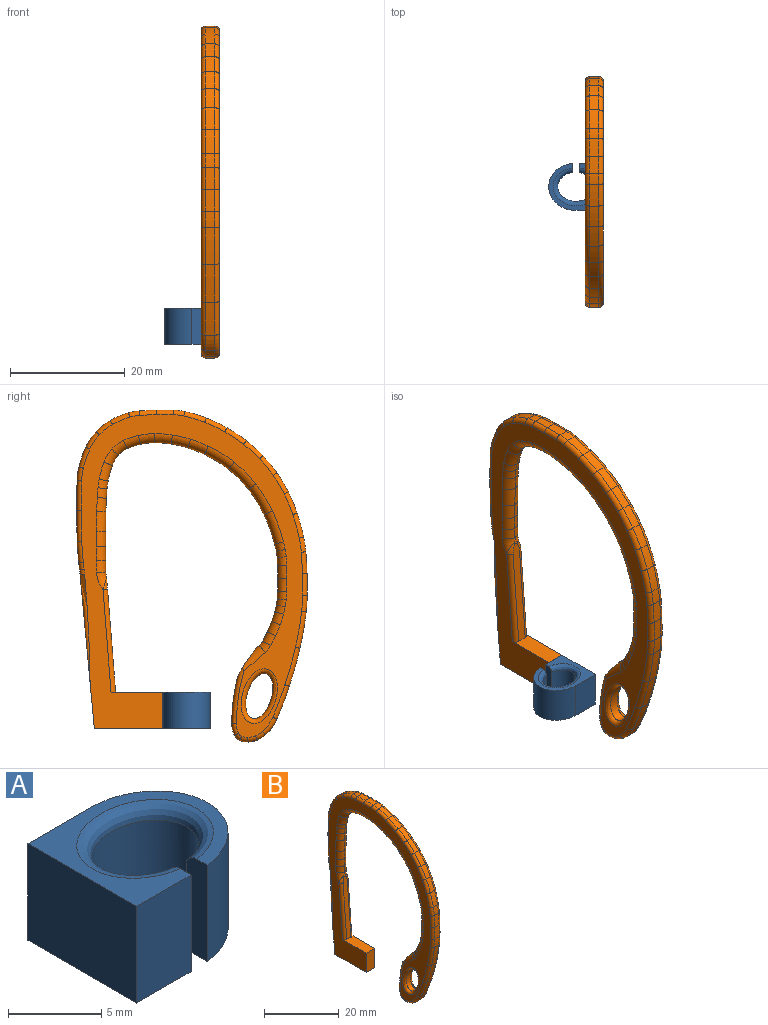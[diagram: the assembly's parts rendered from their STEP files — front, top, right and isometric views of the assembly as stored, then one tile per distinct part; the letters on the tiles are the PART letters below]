
ASSEMBLY  parts=2 mates=1
PART A: 10 faces, bbox 9.6x8.3x6.4 mm
  f0: plane 6.4x1.68mm, normal (1,0,0), area 10.3mm2, adj f1,f6,f7,f8,f9
  f1: extruded ~6.33x5.56mm, area 93mm2, adj f0,f2,f8,f9
  f2: plane 6.4x1.65mm, normal (-1,0,0), area 10mm2, adj f1,f3,f7,f8,f9
  f3: extruded ~8.22x6.35mm, area 84.7mm2, adj f2,f4,f7,f8
  f4: plane 6.35x4.76mm, normal (0,1,0), area 30.2mm2, adj f3,f5,f7,f8
  f5: plane 8.26x6.35mm, normal (-1,0,0), area 52.4mm2, adj f4,f6,f7,f8
  f6: plane 6.35x4.13mm, normal (0,-1,0), area 26.2mm2, adj f0,f5,f7,f8
  f7: plane 9.53x8.26mm, normal (0,0,1), area 27.6mm2, adj f0,f2,f3,f4,f5,f6,f9
  f8: plane 9.53x8.26mm, normal (0,0,-1), area 42.8mm2, adj f0,f1,f2,f3,f4,f5,f6
  f9: bspline ~7.95x6.67mm, area 23.2mm2, adj f0,f1,f2,f7
PART B: 200 faces, bbox 3.8x40.5x58.5 mm
  f0: plane 26.17x3.41mm, normal (0,1,-0.09), area 72.5mm2, adj f1,f47,f48,f49,f124,f157
  f1: cylinder r=232.47mm len=1.59mm, axis (-1,0,0), area 1.3mm2, adj f0,f2,f124,f157
  f2: cylinder r=58.84mm len=1.59mm, axis (-1,0,0), area 1.5mm2, adj f1,f3,f126,f158
  f3: cylinder r=110.76mm len=1.59mm, axis (-1,0,0), area 1.8mm2, adj f2,f4,f128,f159
  f4: cylinder r=45.01mm len=3.81mm, axis (-1,0,0), area 6.1mm2, adj f3,f5,f130,f160
  f5: cylinder r=168.97mm len=5.36mm, axis (-1,0,0), area 8.5mm2, adj f4,f6,f132,f161
  f6: cylinder r=210.56mm len=5.24mm, axis (-1,0,0), area 8.3mm2, adj f5,f7,f134,f162
  f7: cylinder r=11.54mm len=2.35mm, axis (-1,0,0), area 3.8mm2, adj f6,f8,f136,f163
  f8: cylinder r=18.11mm len=3.5mm, axis (-1,0,0), area 5.9mm2, adj f7,f9,f138,f164
  f9: cylinder r=10.63mm len=2.69mm, axis (-1,0,0), area 5.2mm2, adj f8,f10,f140,f165
  f10: cylinder r=9.99mm len=2.47mm, axis (-1,0,0), area 5mm2, adj f9,f11,f142,f166
  f11: cylinder r=14.59mm len=3.2mm, axis (-1,0,0), area 5.5mm2, adj f10,f12,f144,f167
  f12: cylinder r=9.3mm len=1.84mm, axis (-1,0,0), area 3mm2, adj f11,f13,f146,f168
  f13: cylinder r=58.67mm len=3.02mm, axis (-1,0,0), area 4.8mm2, adj f12,f14,f148,f169
  f14: cylinder r=58.13mm len=3.04mm, axis (-1,0,0), area 4.8mm2, adj f13,f15,f150,f170
  f15: cylinder r=10.16mm len=1.91mm, axis (-1,0,0), area 3.1mm2, adj f14,f16,f152,f171
  f16: cylinder r=25.74mm len=3.75mm, axis (-1,0,0), area 6.2mm2, adj f15,f17,f154,f172
  f17: cylinder r=28.28mm len=3.63mm, axis (-1,0,0), area 6.4mm2, adj f16,f18,f156,f173
  f18: cylinder r=28.2mm len=3.34mm, axis (-1,0,0), area 6.4mm2, adj f17,f19,f155,f174
  f19: cylinder r=25.35mm len=2.9mm, axis (-1,0,0), area 6.2mm2, adj f18,f20,f153,f175
  f20: cylinder r=26.11mm len=2.99mm, axis (-1,0,0), area 6.1mm2, adj f19,f21,f151,f176
  f21: cylinder r=26.17mm len=3.32mm, axis (-1,0,0), area 6.1mm2, adj f20,f22,f149,f177
  f22: cylinder r=28.64mm len=3.72mm, axis (-1,0,0), area 6.4mm2, adj f21,f23,f147,f178
  f23: cylinder r=38.83mm len=4.19mm, axis (-1,0,0), area 6.9mm2, adj f22,f24,f145,f179
  f24: cylinder r=19.44mm len=2.55mm, axis (-1,0,0), area 4.1mm2, adj f23,f25,f143,f180
  f25: cylinder r=82.96mm len=3.74mm, axis (-1,0,0), area 5.9mm2, adj f24,f26,f141,f181
  f26: cylinder r=82.89mm len=3.83mm, axis (-1,0,0), area 6.1mm2, adj f25,f27,f139,f182
  f27: cylinder r=28.77mm len=2.92mm, axis (-1,0,0), area 4.6mm2, adj f26,f28,f137,f183
  f28: cylinder r=57.68mm len=6.36mm, axis (-1,0,0), area 10.2mm2, adj f27,f29,f135,f184
  f29: cylinder r=74.7mm len=6.63mm, axis (-1,0,0), area 10.9mm2, adj f28,f30,f133,f185
  f30: cylinder r=71.53mm len=5.73mm, axis (-1,0,0), area 9.7mm2, adj f29,f31,f131,f186
  f31: cylinder r=7.91mm len=2.76mm, axis (-1,0,0), area 5.4mm2, adj f30,f32,f129,f187
  f32: cylinder r=4.84mm len=1.59mm, axis (-1,0,0), area 2.7mm2, adj f31,f33,f127,f188
  f33: cylinder r=4.59mm len=1.63mm, axis (-1,0,0), area 2.7mm2, adj f32,f34,f125,f189
  f34: cylinder r=3.45mm len=1.59mm, axis (-1,0,0), area 2.3mm2, adj f33,f35,f123,f190
  f35: cylinder r=1.84mm len=1.59mm, axis (-1,0,0), area 2mm2, adj f34,f36,f122,f191
  f36: cylinder r=4.49mm len=2.09mm, axis (-1,0,0), area 3.4mm2, adj f35,f37,f121,f192
  f37: cylinder r=34.45mm len=3.69mm, axis (-1,0,0), area 5.9mm2, adj f36,f38,f120,f193
  f38: cylinder r=33.33mm len=3.71mm, axis (-1,0,0), area 6.2mm2, adj f37,f39,f119,f193
  f39: cylinder r=7.14mm len=2.32mm, axis (-1,0,0), area 5mm2, adj f38,f40,f83,f118,f193
  f40: cylinder r=15.1mm len=2.25mm, axis (-1,0,0), area 1.3mm2, adj f39,f41,f83,f116,f117
  f41: plane 2.99x2.51mm, normal (0,0.81,0.59), area 6.9mm2, adj f40,f50,f83,f116
  f42: plane 0.84x0.83mm, normal (0,-0.99,0.17), area 0.3mm2, adj f43,f82,f115,f197,f199
  f43: plane 19.7x1.59mm, normal (0,-1,0.08), area 30.8mm2, adj f42,f44,f196,f197,f198,f199
  f44: plane 9.07x3.2mm, normal (0,0,1), area 26.5mm2, adj f43,f45,f48,f49,f196,f198
  f45: plane 6.32x3.18mm, normal (0,-1,0), area 20.1mm2, adj f44,f47,f48,f49
  f46: extruded ~7.93x4.75mm, area 31.9mm2, adj f194,f195
  f47: plane 11.95x3.18mm, normal (0,0,-1), area 37.9mm2, adj f0,f45,f48,f49
  f48: plane 56.33x38.63mm, normal (1,0,0), area 465.9mm2, adj f0,f44,f45,f47,f50,f51,f52,f53
  f49: plane 56.33x38.63mm, normal (-1,0,0), area 466.1mm2, adj f0,f44,f45,f47,f83,f84,f85,f86
  f50: cylinder r=1.59mm len=4.13mm, axis (0,0.75,-0.67), area 5.9mm2, adj f41,f48,f51,f83,f116
  f51: torus R=4.44mm, axis (1,0,0), area 2.9mm2, adj f48,f50,f52,f84
  f52: torus R=29.43mm, axis (1,0,0), area 4.6mm2, adj f48,f51,f53,f85
  f53: torus R=28.92mm, axis (1,0,0), area 5mm2, adj f48,f52,f54,f86
  f54: torus R=18.86mm, axis (1,0,0), area 4.5mm2, adj f48,f53,f55,f87
  f55: torus R=17.58mm, axis (1,0,0), area 3.1mm2, adj f48,f54,f56,f88
  f56: torus R=12.41mm, axis (1,0,0), area 2.9mm2, adj f48,f55,f57,f89
  f57: torus R=21.42mm, axis (1,0,0), area 3.5mm2, adj f48,f56,f58,f90
  f58: torus R=135.56mm, axis (1,0,0), area 5.6mm2, adj f48,f57,f59,f91
  f59: torus R=133.92mm, axis (1,0,0), area 5.6mm2, adj f48,f58,f60,f92
  f60: torus R=21.45mm, axis (1,0,0), area 3.5mm2, adj f48,f59,f61,f93
  f61: torus R=12.86mm, axis (1,0,0), area 2.9mm2, adj f48,f60,f62,f94
  f62: torus R=19.98mm, axis (1,0,0), area 3.2mm2, adj f48,f61,f63,f95
  f63: torus R=31.27mm, axis (1,0,0), area 14mm2, adj f48,f62,f64,f96
  f64: torus R=24.44mm, axis (1,0,0), area 13.2mm2, adj f48,f63,f65,f97
  f65: torus R=22.66mm, axis (1,0,0), area 12.7mm2, adj f48,f64,f66,f98
  f66: torus R=22.82mm, axis (1,0,0), area 12.7mm2, adj f48,f65,f67,f99
  f67: torus R=25.24mm, axis (1,0,0), area 8mm2, adj f48,f66,f68,f100
  f68: torus R=21.78mm, axis (1,0,0), area 7.7mm2, adj f48,f67,f69,f101
  f69: torus R=19.33mm, axis (1,0,0), area 7.2mm2, adj f48,f68,f70,f102
  f70: torus R=14mm, axis (1,0,0), area 6.7mm2, adj f48,f69,f71,f103
  f71: torus R=12.52mm, axis (1,0,0), area 6.3mm2, adj f48,f70,f72,f104
  f72: torus R=6.19mm, axis (1,0,0), area 5.5mm2, adj f48,f71,f73,f105
  f73: torus R=7.08mm, axis (1,0,0), area 5.7mm2, adj f48,f72,f74,f106
  f74: torus R=20.17mm, axis (1,0,0), area 7.3mm2, adj f48,f73,f75,f107
  f75: torus R=16.03mm, axis (1,0,0), area 3.4mm2, adj f48,f74,f76,f108
  f76: torus R=37.03mm, axis (1,0,0), area 4.2mm2, adj f48,f75,f77,f109
  f77: torus R=75.32mm, axis (1,0,0), area 5.8mm2, adj f48,f76,f78,f110
  f78: torus R=374.9mm, axis (1,0,0), area 8.8mm2, adj f48,f77,f79,f111
  f79: torus R=368.87mm, axis (1,0,0), area 6.7mm2, adj f48,f78,f80,f112
  f80: torus R=230.02mm, axis (1,0,0), area 5.9mm2, adj f48,f79,f81,f113
  f81: torus R=353.05mm, axis (1,0,0), area 5mm2, adj f48,f80,f82,f114
  f82: torus R=4.98mm, axis (1,0,0), area 4.5mm2, adj f42,f48,f81,f115,f199
  f83: cylinder r=1.59mm len=4.8mm, axis (0,-0.75,0.67), area 7.2mm2, adj f39,f40,f41,f49,f50,f84,f193
  f84: torus R=4.44mm, axis (1,0,0), area 2.9mm2, adj f49,f51,f83,f85
  f85: torus R=29.43mm, axis (1,0,0), area 4.6mm2, adj f49,f52,f84,f86
  f86: torus R=28.92mm, axis (1,0,0), area 5mm2, adj f49,f53,f85,f87
  f87: torus R=18.86mm, axis (1,0,0), area 4.5mm2, adj f49,f54,f86,f88
  f88: torus R=17.58mm, axis (1,0,0), area 3.1mm2, adj f49,f55,f87,f89
  f89: torus R=12.41mm, axis (1,0,0), area 2.9mm2, adj f49,f56,f88,f90
  f90: torus R=21.42mm, axis (1,0,0), area 3.5mm2, adj f49,f57,f89,f91
  f91: torus R=135.56mm, axis (1,0,0), area 5.6mm2, adj f49,f58,f90,f92
  f92: torus R=133.92mm, axis (1,0,0), area 5.6mm2, adj f49,f59,f91,f93
  f93: torus R=21.45mm, axis (1,0,0), area 3.5mm2, adj f49,f60,f92,f94
  f94: torus R=12.86mm, axis (1,0,0), area 2.9mm2, adj f49,f61,f93,f95
  f95: torus R=19.98mm, axis (1,0,0), area 3.2mm2, adj f49,f62,f94,f96
  f96: torus R=31.27mm, axis (1,0,0), area 14mm2, adj f49,f63,f95,f97
  f97: torus R=24.44mm, axis (1,0,0), area 13.2mm2, adj f49,f64,f96,f98
  f98: torus R=22.66mm, axis (1,0,0), area 12.7mm2, adj f49,f65,f97,f99
  f99: torus R=22.82mm, axis (1,0,0), area 12.7mm2, adj f49,f66,f98,f100
  f100: torus R=25.24mm, axis (1,0,0), area 8mm2, adj f49,f67,f99,f101
  f101: torus R=21.78mm, axis (1,0,0), area 7.7mm2, adj f49,f68,f100,f102
  f102: torus R=19.33mm, axis (1,0,0), area 7.2mm2, adj f49,f69,f101,f103
  f103: torus R=14mm, axis (1,0,0), area 6.7mm2, adj f49,f70,f102,f104
  f104: torus R=12.52mm, axis (1,0,0), area 6.3mm2, adj f49,f71,f103,f105
  f105: torus R=6.19mm, axis (1,0,0), area 5.5mm2, adj f49,f72,f104,f106
  f106: torus R=7.08mm, axis (1,0,0), area 5.7mm2, adj f49,f73,f105,f107
  f107: torus R=20.17mm, axis (1,0,0), area 7.3mm2, adj f49,f74,f106,f108
  f108: torus R=16.03mm, axis (1,0,0), area 3.4mm2, adj f49,f75,f107,f109
  f109: torus R=37.03mm, axis (1,0,0), area 4.2mm2, adj f49,f76,f108,f110
  f110: torus R=75.32mm, axis (1,0,0), area 5.8mm2, adj f49,f77,f109,f111
  f111: torus R=374.9mm, axis (1,0,0), area 8.8mm2, adj f49,f78,f110,f112
  f112: torus R=368.87mm, axis (1,0,0), area 6.7mm2, adj f49,f79,f111,f113
  f113: torus R=230.02mm, axis (1,0,0), area 5.9mm2, adj f49,f80,f112,f114
  f114: torus R=353.05mm, axis (1,0,0), area 5mm2, adj f49,f81,f113,f115
  f115: torus R=4.98mm, axis (1,0,0), area 4.5mm2, adj f42,f49,f82,f114,f197
  f116: bspline ~3.25x1.72mm, area 1.2mm2, adj f40,f41,f50,f117
  f117: torus R=15.9mm, axis (1,0,0), area 0.6mm2, adj f40,f48,f116,f118
  f118: torus R=6.35mm, axis (1,0,0), area 3mm2, adj f39,f48,f117,f119
  f119: torus R=32.54mm, axis (1,0,0), area 4.7mm2, adj f38,f48,f118,f120
  f120: torus R=33.66mm, axis (1,0,0), area 4.6mm2, adj f37,f48,f119,f121
  f121: torus R=3.69mm, axis (1,0,0), area 2.5mm2, adj f36,f48,f120,f122
  f122: torus R=1.05mm, axis (1,0,0), area 1.3mm2, adj f35,f48,f121,f123
  f123: torus R=2.65mm, axis (1,0,0), area 1.7mm2, adj f34,f48,f122,f125
  f124: torus R=233.27mm, axis (1,0,0), area 12.2mm2, adj f0,f1,f48,f126
  f125: torus R=3.79mm, axis (1,0,0), area 2mm2, adj f33,f48,f123,f127
  f126: torus R=59.64mm, axis (1,0,0), area 1.2mm2, adj f2,f48,f124,f128
  f127: torus R=4.05mm, axis (1,0,0), area 2mm2, adj f32,f48,f125,f129
  f128: torus R=111.55mm, axis (1,0,0), area 1.4mm2, adj f3,f48,f126,f130
  f129: torus R=7.12mm, axis (1,0,0), area 4.1mm2, adj f31,f48,f127,f131
  f130: torus R=44.22mm, axis (1,0,0), area 4.7mm2, adj f4,f48,f128,f132
  f131: torus R=70.74mm, axis (1,0,0), area 7.6mm2, adj f30,f48,f129,f133
  f132: torus R=168.18mm, axis (1,0,0), area 6.7mm2, adj f5,f48,f130,f134
  f133: torus R=73.9mm, axis (1,0,0), area 8.6mm2, adj f29,f48,f131,f135
  f134: torus R=209.77mm, axis (1,0,0), area 6.5mm2, adj f6,f48,f132,f136
  f135: torus R=56.88mm, axis (1,0,0), area 8mm2, adj f28,f48,f133,f137
  f136: torus R=10.75mm, axis (1,0,0), area 2.9mm2, adj f7,f48,f134,f138
  f137: torus R=27.97mm, axis (1,0,0), area 3.6mm2, adj f27,f48,f135,f139
  f138: torus R=17.31mm, axis (1,0,0), area 4.6mm2, adj f8,f48,f136,f140
  f139: torus R=82.1mm, axis (1,0,0), area 4.8mm2, adj f26,f48,f137,f141
  f140: torus R=9.84mm, axis (1,0,0), area 3.9mm2, adj f9,f48,f138,f142
  f141: torus R=82.17mm, axis (1,0,0), area 4.7mm2, adj f25,f48,f139,f143
  f142: torus R=9.2mm, axis (1,0,0), area 3.8mm2, adj f10,f48,f140,f144
  f143: torus R=18.65mm, axis (1,0,0), area 3.2mm2, adj f24,f48,f141,f145
  f144: torus R=13.79mm, axis (1,0,0), area 4.2mm2, adj f11,f48,f142,f146
  f145: torus R=38.03mm, axis (1,0,0), area 5.4mm2, adj f23,f48,f143,f147
  f146: torus R=8.5mm, axis (1,0,0), area 2.3mm2, adj f12,f48,f144,f148
  f147: torus R=27.85mm, axis (1,0,0), area 5mm2, adj f22,f48,f145,f149
  f148: torus R=57.87mm, axis (1,0,0), area 3.8mm2, adj f13,f48,f146,f150
  f149: torus R=25.38mm, axis (1,0,0), area 4.8mm2, adj f21,f48,f147,f151
  f150: torus R=57.33mm, axis (1,0,0), area 3.8mm2, adj f14,f48,f148,f152
  f151: torus R=25.32mm, axis (1,0,0), area 4.8mm2, adj f20,f48,f149,f153
  f152: torus R=9.37mm, axis (1,0,0), area 2.3mm2, adj f15,f48,f150,f154
  f153: torus R=24.56mm, axis (1,0,0), area 4.8mm2, adj f19,f48,f151,f155
  f154: torus R=24.95mm, axis (1,0,0), area 4.8mm2, adj f16,f48,f152,f156
  f155: torus R=27.4mm, axis (1,0,0), area 5mm2, adj f18,f48,f153,f156
  f156: torus R=27.49mm, axis (1,0,0), area 5mm2, adj f17,f48,f154,f155
  f157: torus R=233.27mm, axis (1,0,0), area 12.2mm2, adj f0,f1,f49,f158
  f158: torus R=59.64mm, axis (1,0,0), area 1.2mm2, adj f2,f49,f157,f159
  f159: torus R=111.55mm, axis (1,0,0), area 1.4mm2, adj f3,f49,f158,f160
  f160: torus R=44.22mm, axis (1,0,0), area 4.7mm2, adj f4,f49,f159,f161
  f161: torus R=168.18mm, axis (1,0,0), area 6.7mm2, adj f5,f49,f160,f162
  f162: torus R=209.77mm, axis (1,0,0), area 6.5mm2, adj f6,f49,f161,f163
  f163: torus R=10.75mm, axis (1,0,0), area 2.9mm2, adj f7,f49,f162,f164
  f164: torus R=17.31mm, axis (1,0,0), area 4.6mm2, adj f8,f49,f163,f165
  f165: torus R=9.84mm, axis (1,0,0), area 3.9mm2, adj f9,f49,f164,f166
  f166: torus R=9.2mm, axis (1,0,0), area 3.8mm2, adj f10,f49,f165,f167
  f167: torus R=13.79mm, axis (1,0,0), area 4.2mm2, adj f11,f49,f166,f168
  f168: torus R=8.5mm, axis (1,0,0), area 2.3mm2, adj f12,f49,f167,f169
  f169: torus R=57.87mm, axis (1,0,0), area 3.8mm2, adj f13,f49,f168,f170
  f170: torus R=57.33mm, axis (1,0,0), area 3.8mm2, adj f14,f49,f169,f171
  f171: torus R=9.37mm, axis (1,0,0), area 2.3mm2, adj f15,f49,f170,f172
  f172: torus R=24.95mm, axis (1,0,0), area 4.8mm2, adj f16,f49,f171,f173
  f173: torus R=27.49mm, axis (1,0,0), area 5mm2, adj f17,f49,f172,f174
  f174: torus R=27.4mm, axis (1,0,0), area 5mm2, adj f18,f49,f173,f175
  f175: torus R=24.56mm, axis (1,0,0), area 4.8mm2, adj f19,f49,f174,f176
  f176: torus R=25.32mm, axis (1,0,0), area 4.8mm2, adj f20,f49,f175,f177
  f177: torus R=25.38mm, axis (1,0,0), area 4.8mm2, adj f21,f49,f176,f178
  f178: torus R=27.85mm, axis (1,0,0), area 5mm2, adj f22,f49,f177,f179
  f179: torus R=38.03mm, axis (1,0,0), area 5.4mm2, adj f23,f49,f178,f180
  f180: torus R=18.65mm, axis (1,0,0), area 3.2mm2, adj f24,f49,f179,f181
  f181: torus R=82.17mm, axis (1,0,0), area 4.7mm2, adj f25,f49,f180,f182
  f182: torus R=82.1mm, axis (1,0,0), area 4.8mm2, adj f26,f49,f181,f183
  f183: torus R=27.97mm, axis (1,0,0), area 3.6mm2, adj f27,f49,f182,f184
  f184: torus R=56.88mm, axis (1,0,0), area 8mm2, adj f28,f49,f183,f185
  f185: torus R=73.9mm, axis (1,0,0), area 8.6mm2, adj f29,f49,f184,f186
  f186: torus R=70.74mm, axis (1,0,0), area 7.6mm2, adj f30,f49,f185,f187
  f187: torus R=7.12mm, axis (1,0,0), area 4.1mm2, adj f31,f49,f186,f188
  f188: torus R=4.05mm, axis (1,0,0), area 2mm2, adj f32,f49,f187,f189
  f189: torus R=3.79mm, axis (1,0,0), area 2mm2, adj f33,f49,f188,f190
  f190: torus R=2.65mm, axis (1,0,0), area 1.7mm2, adj f34,f49,f189,f191
  f191: torus R=1.05mm, axis (1,0,0), area 1.3mm2, adj f35,f49,f190,f192
  f192: torus R=3.69mm, axis (1,0,0), area 2.5mm2, adj f36,f49,f191,f193
  f193: torus R=33.66mm, axis (1,0,0), area 10.9mm2, adj f37,f38,f39,f49,f83,f192
  f194: bspline ~9.53x6.35mm, area 27.3mm2, adj f46,f49
  f195: bspline ~9.53x6.35mm, area 27.3mm2, adj f46,f48
  f196: cylinder r=0.79mm len=18mm, axis (0,-0.08,-1), area 22.4mm2, adj f43,f44,f49,f197
  f197: bspline ~2.5x1.56mm, area 1.7mm2, adj f42,f43,f115,f196
  f198: cylinder r=0.79mm len=18mm, axis (0,0.08,1), area 22.4mm2, adj f43,f44,f48,f199
  f199: bspline ~2.5x1.56mm, area 1.7mm2, adj f42,f43,f82,f198
PLACE A rot(axis=(0,0,1),180deg) t=(-5.88,2.47,-9.93)mm
PLACE B t=(-4.29,1.52,16.66)mm
MATE fastened A.f6 <-> B.f45  axis (0,1,0) through (-1.12,6.6,-6.75)mm
